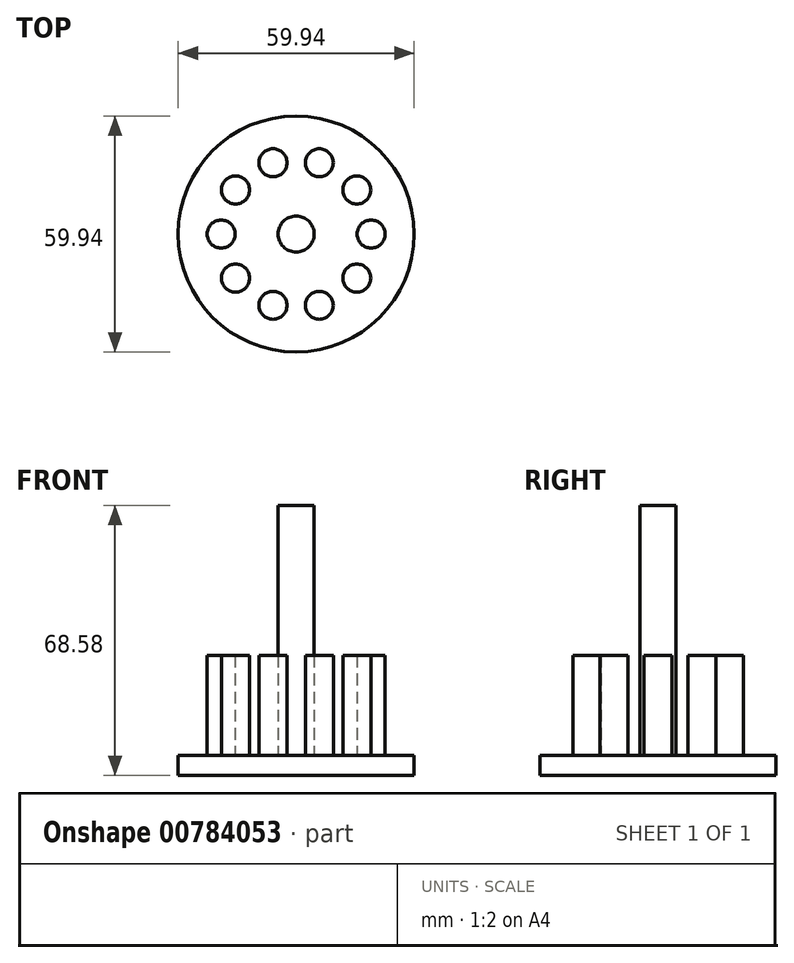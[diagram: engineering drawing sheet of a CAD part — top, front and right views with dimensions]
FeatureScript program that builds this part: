
annotation { "Feature Type Name" : "Feature", "Feature Type Description" : "" }
export const myFeature = defineFeature(function(context is Context, id is Id, definition is map)
    precondition{}
    {
        {
            var Q0;
            Q0=qCreatedBy(makeId("Top.planeOp"),FACE);
            var sketch = newSketch(context, id + "F0", { "sketchPlane" : qUnion([Q0])});
            skCircle(sketch, "E0", {"center": v(0, 0) * mm, "radius": 29.97 * mm});
            skSolve(sketch);
        }
        {
            var Q0;
            Q0=makeQuery(id+"F0.imprint","IMPRINT",FACE,{"disambiguationData":[TD([[makeQuery(id+"F0.imprint","IMPRINT",EDGE,{"derivedFrom":sQuery(id+"F0.wireOp",EDGE,"E0")}),1.0]])]});
            extrude(context, id + "F1", {"entities" : qUnion([Q0]), "depth" : 5.08 * mm, "offsetDistance" : 25.4 * mm});
        }
        {
            var Q0;
            Q0=makeQuery(id+"F1.opExtrude","CAP_FACE",FACE,{"disambiguationData":[OSD([sQuery(id+"F0.wireOp",EDGE,"E0")])],"isStart":false});
            var sketch = newSketch(context, id + "F2", { "sketchPlane" : qUnion([Q0])});
            skCircle(sketch, "E1", {"center": v(-19.05, 0) * mm, "radius": 3.56 * mm});
            skSolve(sketch);
        }
        {
            var Q0;
            Q0 = qSketchRegion(id + "F2", true);
            extrude(context, id + "F3", {"entities" : qUnion([Q0]), "operationType" : NewBodyOperationType.ADD, "depth" : 25.4 * mm, "offsetDistance" : 25.4 * mm});
        }
        {
            var Q0;
            Q0=makeQuery(id+"F1.opExtrude","SWEPT_BODY",BODY,{"disambiguationData":[OSD([sQuery(id+"F0.wireOp",EDGE,"E0")])]});
            var Q1;
            Q1=makeQuery(id+"F1.opExtrude","CAP_EDGE",EDGE,{"disambiguationData":[OSD([sQuery(id+"F0.wireOp",EDGE,"E0")])],"isStart":false});
            circularPattern(context, id + "F4", {"entities" : qUnion([Q0]), "axis" : qUnion([Q1]), "angle" : 360 * degree, "instanceCount" : 10, "oppositeDirection" : true, "equalSpace" : true});
        }
        {
            var Q0;
            Q0=makeQuery(id+"F1.opExtrude","CAP_FACE",FACE,{"disambiguationData":[OSD([sQuery(id+"F0.wireOp",EDGE,"E0")])],"isStart":false});
            var sketch = newSketch(context, id + "F5", { "sketchPlane" : qUnion([Q0])});
            skCircle(sketch, "E2", {"center": v(0, 0) * mm, "radius": 4.57 * mm});
            skSolve(sketch);
        }
        {
            var Q0;
            Q0=makeQuery(id+"F5.imprint","IMPRINT",FACE,{"disambiguationData":[TD([[makeQuery(id+"F5.imprint","IMPRINT",EDGE,{"derivedFrom":sQuery(id+"F5.wireOp",EDGE,"E2")}),1.0]])]});
            extrude(context, id + "F6", {"entities" : qUnion([Q0]), "operationType" : NewBodyOperationType.ADD, "depth" : 63.5 * mm, "offsetDistance" : 25.4 * mm});
        }
        {
            var Q0;
            Q0=sQuery(id+"F2.wireOp",EDGE,"E1");
            extrude(context, id + "F7", {"bodyType" : ToolBodyType.SURFACE, "surfaceEntities" : qUnion([Q0]), "depth" : 25.4 * mm, "offsetDistance" : 25.4 * mm});
        }
    });
